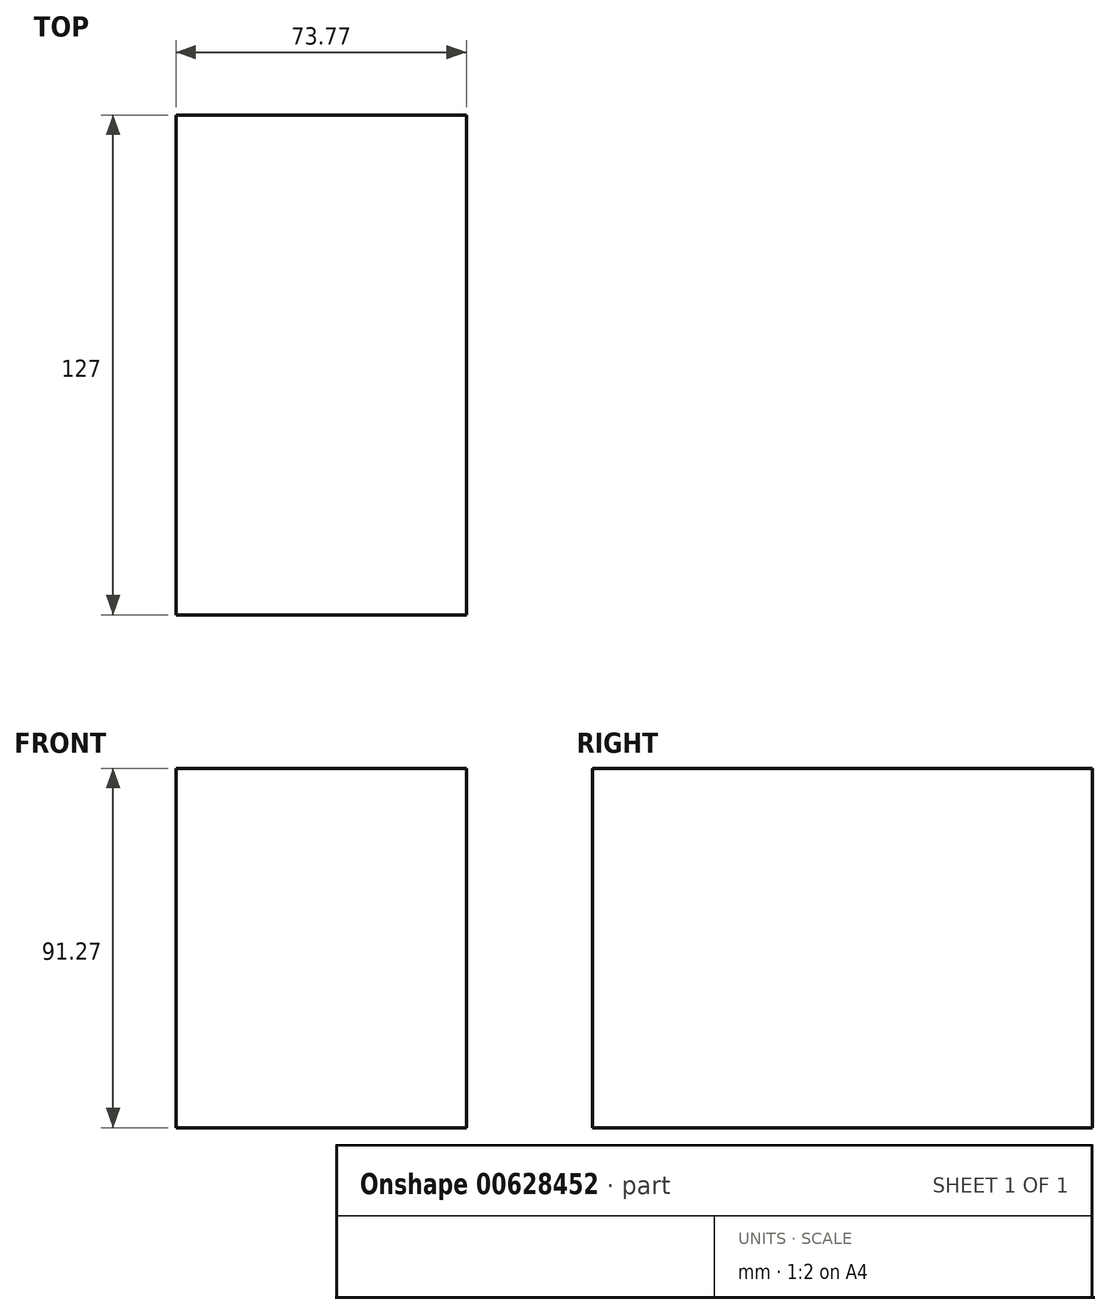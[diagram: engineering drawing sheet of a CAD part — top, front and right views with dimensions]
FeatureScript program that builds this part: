
annotation { "Feature Type Name" : "Feature", "Feature Type Description" : "" }
export const myFeature = defineFeature(function(context is Context, id is Id, definition is map)
    precondition{}
    {
        {
            var Q0;
            Q0=qCreatedBy(makeId("Front.planeOp"),FACE);
            var sketch = newSketch(context, id + "F0", { "sketchPlane" : qUnion([Q0])});
            skLineSegment(sketch, "E0.bottom", {"start": v(73.77, 91.27) * mm, "end": v(0, 91.27) * mm});
            skLineSegment(sketch, "E0.top", {"start": v(73.77, 0) * mm, "end": v(0, 0) * mm});
            skLineSegment(sketch, "E0.left", {"start": v(73.77, 91.27) * mm, "end": v(73.77, 0) * mm});
            skLineSegment(sketch, "E0.right", {"start": v(0, 91.27) * mm, "end": v(0, 0) * mm});
            skSolve(sketch);
        }
        {
            var Q0;
            Q0 = qSketchRegion(id + "F0", true);
            extrude(context, id + "F1", {"entities" : qUnion([Q0]), "depth" : 127 * mm, "offsetDistance" : 25.4 * mm});
        }
    });
